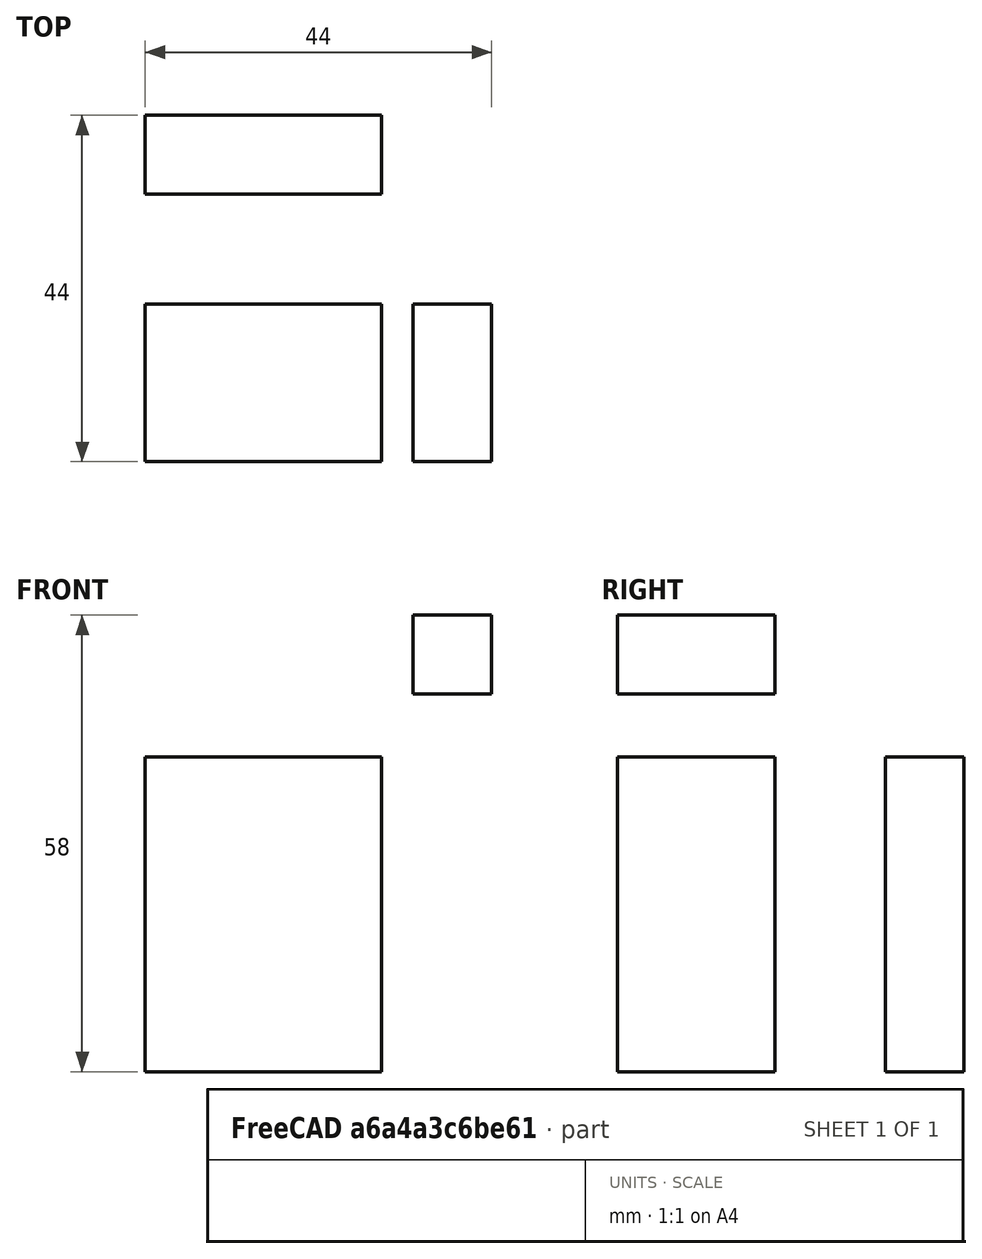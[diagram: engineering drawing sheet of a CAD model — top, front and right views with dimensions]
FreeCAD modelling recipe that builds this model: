
FCSTD DOCUMENT  (FreeCAD 0.17R13509 (Git))
Label: mode12_tns_mode3
License: All rights reserved
LicenseURL: http://en.wikipedia.org/wiki/All_rights_reserved
objects: Part::Box×38, Part::MultiFuse×17
note: 55 computed .brp shape members not serialized (recipe doc carries the construction recipe); baked Part::Feature solids carry a one-line shape summary decoded from their .brp

FEATURE [Part::Box] Box010  label="Cube010"
  AttacherType = Attacher::AttachEngine3D
  Height = 10
  Length = 10
  Placement = pos=(14,0,30) rot=(0,0,1;0rad)
  Width = 10
FEATURE [Part::Box] Box007  label="Cube007"
  AttacherType = Attacher::AttachEngine3D
  Height = 10
  Length = 10
  Placement = pos=(14,0,30) rot=(0,0,1;0rad)
  Width = 10
FEATURE [Part::Box] Box009  label="Cube009"
  AttacherType = Attacher::AttachEngine3D
  Height = 10
  Length = 10
  Placement = pos=(34,0,30) rot=(0,0,1;0rad)
  Width = 10
FEATURE [Part::Box] Box012  label="Cube012"
  AttacherType = Attacher::AttachEngine3D
  Height = 10
  Length = 10
  Placement = pos=(24,0,30) rot=(0,0,1;0rad)
  Width = 10
FEATURE [Part::Box] Box008  label="Cube008"
  AttacherType = Attacher::AttachEngine3D
  Height = 10
  Length = 10
  Placement = pos=(24,0,30) rot=(0,0,1;0rad)
  Width = 10
FEATURE [Part::MultiFuse] Fusion002
  Shapes = -> [Box007,Box008,Box009]
FEATURE [Part::Box] Box011  label="Cube011"
  AttacherType = Attacher::AttachEngine3D
  Height = 10
  Length = 10
  Placement = pos=(34,0,30) rot=(0,0,1;0rad)
  Width = 10
FEATURE [Part::MultiFuse] Fusion003
  Placement = pos=(0,0,-10) rot=(0,0,1;0rad)
  Shapes = -> [Box010,Box012,Box011]
FEATURE [Part::Box] Box014  label="Cube014"
  AttacherType = Attacher::AttachEngine3D
  Height = 10
  Length = 10
  Placement = pos=(34,0,30) rot=(0,0,1;0rad)
  Width = 10
FEATURE [Part::Box] Box013  label="Cube013"
  AttacherType = Attacher::AttachEngine3D
  Height = 10
  Length = 10
  Placement = pos=(14,0,30) rot=(0,0,1;0rad)
  Width = 10
FEATURE [Part::Box] Box015  label="Cube015"
  AttacherType = Attacher::AttachEngine3D
  Height = 10
  Length = 10
  Placement = pos=(24,0,30) rot=(0,0,1;0rad)
  Width = 10
FEATURE [Part::Box] Box017  label="Cube017"
  AttacherType = Attacher::AttachEngine3D
  Height = 10
  Length = 10
  Placement = pos=(34,0,30) rot=(0,0,1;0rad)
  Width = 10
FEATURE [Part::Box] Box016  label="Cube016"
  AttacherType = Attacher::AttachEngine3D
  Height = 10
  Length = 10
  Placement = pos=(14,0,30) rot=(0,0,1;0rad)
  Width = 10
FEATURE [Part::Box] Box018  label="Cube018"
  AttacherType = Attacher::AttachEngine3D
  Height = 10
  Length = 10
  Placement = pos=(24,0,30) rot=(0,0,1;0rad)
  Width = 10
FEATURE [Part::MultiFuse] Fusion005
  Placement = pos=(0,0,-30) rot=(0,0,1;0rad)
  Shapes = -> [Box016,Box018,Box017]
FEATURE [Part::MultiFuse] Fusion004
  Placement = pos=(0,0,-20) rot=(0,0,1;0rad)
  Shapes = -> [Box013,Box015,Box014]
FEATURE [Part::MultiFuse] Fusion006  label="Mode12"
  Placement = pos=(0,10,0) rot=(0,0,1;0rad)
  Shapes = -> [Fusion002,Fusion003,Fusion005,Fusion004]
FEATURE [Part::Box] Box019  label="Cube019"
  AttacherType = Attacher::AttachEngine3D
  Height = 10
  Length = 10
  Placement = pos=(28,0,10) rot=(0,0,1;0rad)
  Width = 10
FEATURE [Part::Box] Box020  label="Cube020"
  AttacherType = Attacher::AttachEngine3D
  Height = 10
  Length = 10
  Placement = pos=(28,0,0) rot=(0,0,1;0rad)
  Width = 10
FEATURE [Part::MultiFuse] Fusion007  label="Mode 3"
  Placement = pos=(48,-4,86) rot=(0.57735,0.57735,-0.57735;2.0944rad)
  Shapes = -> [Box019,Box020]
FEATURE [Part::Box] Box021  label="Cube021"
  AttacherType = Attacher::AttachEngine3D
  Height = 10
  Length = 10
  Placement = pos=(34,0,30) rot=(0,0,1;0rad)
  Width = 10
FEATURE [Part::Box] Box022  label="Cube022"
  AttacherType = Attacher::AttachEngine3D
  Height = 10
  Length = 10
  Placement = pos=(14,0,30) rot=(0,0,1;0rad)
  Width = 10
FEATURE [Part::Box] Box023  label="Cube023"
  AttacherType = Attacher::AttachEngine3D
  Height = 10
  Length = 10
  Placement = pos=(14,0,30) rot=(0,0,1;0rad)
  Width = 10
FEATURE [Part::Box] Box024  label="Cube024"
  AttacherType = Attacher::AttachEngine3D
  Height = 10
  Length = 10
  Placement = pos=(24,0,30) rot=(0,0,1;0rad)
  Width = 10
FEATURE [Part::Box] Box025  label="Cube025"
  AttacherType = Attacher::AttachEngine3D
  Height = 10
  Length = 10
  Placement = pos=(24,0,30) rot=(0,0,1;0rad)
  Width = 10
FEATURE [Part::MultiFuse] Fusion012
  Shapes = -> [Box022,Box025,Box021]
FEATURE [Part::Box] Box026  label="Cube026"
  AttacherType = Attacher::AttachEngine3D
  Height = 10
  Length = 10
  Placement = pos=(34,0,30) rot=(0,0,1;0rad)
  Width = 10
FEATURE [Part::MultiFuse] Fusion011
  Placement = pos=(0,0,-10) rot=(0,0,1;0rad)
  Shapes = -> [Box023,Box024,Box026]
FEATURE [Part::Box] Box027  label="Cube027"
  AttacherType = Attacher::AttachEngine3D
  Height = 10
  Length = 10
  Placement = pos=(34,0,30) rot=(0,0,1;0rad)
  Width = 10
FEATURE [Part::Box] Box028  label="Cube028"
  AttacherType = Attacher::AttachEngine3D
  Height = 10
  Length = 10
  Placement = pos=(14,0,30) rot=(0,0,1;0rad)
  Width = 10
FEATURE [Part::Box] Box029  label="Cube029"
  AttacherType = Attacher::AttachEngine3D
  Height = 10
  Length = 10
  Placement = pos=(24,0,30) rot=(0,0,1;0rad)
  Width = 10
FEATURE [Part::MultiFuse] Fusion008
  Placement = pos=(0,0,-20) rot=(0,0,1;0rad)
  Shapes = -> [Box028,Box029,Box027]
FEATURE [Part::Box] Box030  label="Cube030"
  AttacherType = Attacher::AttachEngine3D
  Height = 10
  Length = 10
  Placement = pos=(34,0,30) rot=(0,0,1;0rad)
  Width = 10
FEATURE [Part::Box] Box031  label="Cube031"
  AttacherType = Attacher::AttachEngine3D
  Height = 10
  Length = 10
  Placement = pos=(14,0,30) rot=(0,0,1;0rad)
  Width = 10
FEATURE [Part::Box] Box032  label="Cube032"
  AttacherType = Attacher::AttachEngine3D
  Height = 10
  Length = 10
  Placement = pos=(24,0,30) rot=(0,0,1;0rad)
  Width = 10
FEATURE [Part::MultiFuse] Fusion009
  Placement = pos=(0,0,-30) rot=(0,0,1;0rad)
  Shapes = -> [Box031,Box032,Box030]
FEATURE [Part::MultiFuse] Fusion010  label="Mode013"
  Placement = pos=(0,-14,0) rot=(0,0,1;0rad)
  Shapes = -> [Fusion012,Fusion011,Fusion009,Fusion008]
FEATURE [Part::Box] Box033  label="Cube033"
  AttacherType = Attacher::AttachEngine3D
  Height = 10
  Length = 10
  Placement = pos=(34,0,30) rot=(0,0,1;0rad)
  Width = 10
FEATURE [Part::Box] Box034  label="Cube034"
  AttacherType = Attacher::AttachEngine3D
  Height = 10
  Length = 10
  Placement = pos=(24,0,30) rot=(0,0,1;0rad)
  Width = 10
FEATURE [Part::Box] Box035  label="Cube035"
  AttacherType = Attacher::AttachEngine3D
  Height = 10
  Length = 10
  Placement = pos=(14,0,30) rot=(0,0,1;0rad)
  Width = 10
FEATURE [Part::Box] Box036  label="Cube036"
  AttacherType = Attacher::AttachEngine3D
  Height = 10
  Length = 10
  Placement = pos=(14,0,30) rot=(0,0,1;0rad)
  Width = 10
FEATURE [Part::Box] Box037  label="Cube037"
  AttacherType = Attacher::AttachEngine3D
  Height = 10
  Length = 10
  Placement = pos=(34,0,30) rot=(0,0,1;0rad)
  Width = 10
FEATURE [Part::Box] Box038  label="Cube038"
  AttacherType = Attacher::AttachEngine3D
  Height = 10
  Length = 10
  Placement = pos=(14,0,30) rot=(0,0,1;0rad)
  Width = 10
FEATURE [Part::Box] Box039  label="Cube039"
  AttacherType = Attacher::AttachEngine3D
  Height = 10
  Length = 10
  Placement = pos=(24,0,30) rot=(0,0,1;0rad)
  Width = 10
FEATURE [Part::Box] Box040  label="Cube040"
  AttacherType = Attacher::AttachEngine3D
  Height = 10
  Length = 10
  Placement = pos=(14,0,30) rot=(0,0,1;0rad)
  Width = 10
FEATURE [Part::MultiFuse] Fusion016
  Placement = pos=(0,0,-20) rot=(0,0,1;0rad)
  Shapes = -> [Box040,Box034,Box033]
FEATURE [Part::Box] Box041  label="Cube041"
  AttacherType = Attacher::AttachEngine3D
  Height = 10
  Length = 10
  Placement = pos=(24,0,30) rot=(0,0,1;0rad)
  Width = 10
FEATURE [Part::Box] Box042  label="Cube042"
  AttacherType = Attacher::AttachEngine3D
  Height = 10
  Length = 10
  Placement = pos=(34,0,30) rot=(0,0,1;0rad)
  Width = 10
FEATURE [Part::MultiFuse] Fusion013
  Placement = pos=(0,0,-30) rot=(0,0,1;0rad)
  Shapes = -> [Box036,Box039,Box042]
FEATURE [Part::Box] Box043  label="Cube043"
  AttacherType = Attacher::AttachEngine3D
  Height = 10
  Length = 10
  Placement = pos=(34,0,30) rot=(0,0,1;0rad)
  Width = 10
FEATURE [Part::MultiFuse] Fusion015
  Shapes = -> [Box038,Box041,Box043]
FEATURE [Part::Box] Box044  label="Cube044"
  AttacherType = Attacher::AttachEngine3D
  Height = 10
  Length = 10
  Placement = pos=(24,0,30) rot=(0,0,1;0rad)
  Width = 10
FEATURE [Part::MultiFuse] Fusion017
  Placement = pos=(0,0,-10) rot=(0,0,1;0rad)
  Shapes = -> [Box035,Box044,Box037]
FEATURE [Part::MultiFuse] Fusion014  label="Mode014"
  Placement = pos=(0,-24,0) rot=(0,0,1;0rad)
  Shapes = -> [Fusion015,Fusion017,Fusion013,Fusion016]
FEATURE [Part::MultiFuse] Fusion  label="Mode123"
  Shapes = -> [Fusion014,Fusion010]
